# Revit family: 2059109
name_source: partatom
category: Lighting Fixtures
revit_build: Autodesk Revit 2018 (Build: 20170223_1515(x64)
units: mm (PartAtom-declared; Revit-internal decimal feet)

## family parameters
Always vertical = No
Cut with Voids When Loaded = No
Light Source = No
Part Type = Normal
Room Calculation Point = No
Round Connector Dimension = Use Diameter
Shared = No
Work Plane-Based = Yes

## types (1)
- 2059109 BEACON WW LED HO 4K L3 WHT
    Apparent Load = 48 VA
    Assembly Code = D5020200
    Body Material = Aluminum_Sylvania_Beacon_Black
    CRI ( Ra ) = 93
    Catalog Number = 2059065 BEACON WW LED 3K L3 BLK
    Default Elevation = 0 mm  [stored 0 ft]
    Description = 2059109 BEACON WW LED HO 4K L3 WHT  Integrated LED spotlight, white RAL 9016, compact and minimalist design, ideal for museum, gallery and display applications, die-cast aluminium body, passive cooling heatsink, uniform ceiling to floor vertical illuminance up to 4m height and 4.5m horizontal spread, beam angle: asymmetric wallwash, optics: asymmetric glass lens, colour temperature: 4000K warm white, total system power: 48W, total fixture output: 4916lm, luminaire efficacy: 102lm/W, LOR: 100%, colour rendering: Ra 85 typical, LED Chromacity: 3 step MacAdam ellipse, lifetime: 50,000 hours at 70% of the original output (L70), energy class: A++, A+, A, IR/UV free light source without heat radiation, operating voltage: 220-240V / 50-60Hz, drive current: 1200mA, electronic driver, non-dimmable, switched only, power factor: 0.98, electrical protection: CLASS I, 3-circuit track adaptor, suitable for Concord Lytespan 3 track, ingress protection rating: IP20, suitable for internal environment only,  horizontal rotatio...
    Diameter = 113 mm  [stored 0.370735 ft]
    Diffuser Material = Glass_Sylvania_Beacon_Clear_3000K
    Drive Current = 1200mA
    IK Rating = IK02
    IP Rating = IP20
    Initial Color = 4000 K
    Initial Intensity = 2978 lm
    LOR = 1
    Lamp Type = 2059109IES : 2059065
    Life = 50 000h
    Light Loss Factor = 1
    Model = BEACON WW LED HO 4K L3 WHT
    Product Family = BEACON LED WALLWASH
    Reflector Material = Aluminum_Sylvania_Beacon_Bright
    URL = 0.98
    Voltage = 240 V
    Voltage Comments = UNV (Universal Voltage; 220-240 Volt)
    Weight = 1.65 kg

note: [stored X ft] marks values corroborated as IEEE doubles in the binary element streams (Revit-internal decimal feet)

## geometry (parser evidence)
native form markers: Sweep x13
no freeform markers — native parametric forms only
